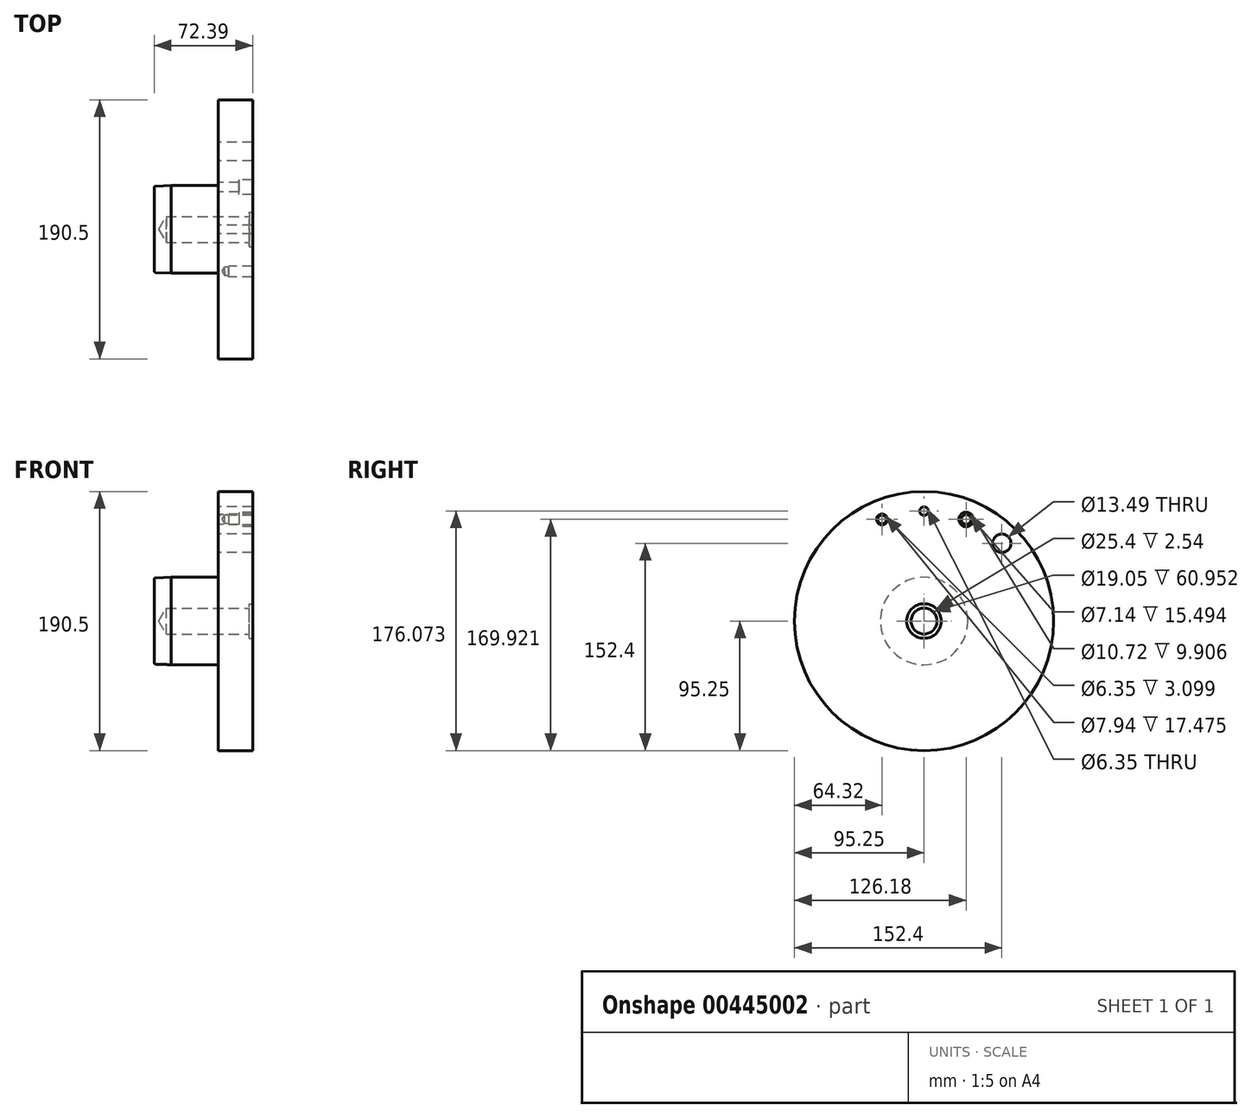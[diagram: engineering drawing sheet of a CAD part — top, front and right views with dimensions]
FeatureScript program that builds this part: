
annotation { "Feature Type Name" : "Feature", "Feature Type Description" : "" }
export const myFeature = defineFeature(function(context is Context, id is Id, definition is map)
    precondition{}
    {
        {
            var Q0;
            Q0=qCreatedBy(makeId("Front.planeOp"),FACE);
            var sketch = newSketch(context, id + "F0", { "sketchPlane" : qUnion([Q0])});
            skLineSegment(sketch, "E0", {"start": v(-46.99, 0) * mm, "end": v(-46.99, 30.46) * mm});
            skArc(sketch, "E1", {"start": v(-47, 30.46) * mm, "mid": v(-46.63, 31.34) * mm, "end": v(-45.76, 31.73) * mm});
            skLineSegment(sketch, "E2", {"start": v(-45.76, 31.73) * mm, "end": v(-34.3, 32.13) * mm});
            skLineSegment(sketch, "E3", {"start": v(-34.29, 32.13) * mm, "end": v(0, 32.13) * mm});
            skLineSegment(sketch, "E4", {"start": v(0, 32.13) * mm, "end": v(0, 95.25) * mm});
            skLineSegment(sketch, "E5", {"start": v(0, 95.25) * mm, "end": v(25.4, 95.25) * mm});
            skLineSegment(sketch, "E6", {"start": v(25.4, 95.25) * mm, "end": v(25.4, 0) * mm});
            skLineSegment(sketch, "E7", {"start": v(25.4, 0) * mm, "end": v(-46.99, 0) * mm});
            skLineSegment(sketch, "E8", {"start": v(0, 0) * mm, "end": v(-66.47, 0) * mm, "construction": true});
            skSolve(sketch);
        }
        {
            var Q0;
            Q0=makeQuery(id+"F0.imprint","IMPRINT",FACE,{"disambiguationData":[TD([[makeQuery(id+"F0.imprint","IMPRINT",EDGE,{"derivedFrom":sQuery(id+"F0.wireOp",EDGE,"E0")}),-1.0]])]});
            var Q1;
            Q1=sQuery(id+"F0.wireOp",EDGE,"E8");
            revolve(context, id + "F1", {"entities" : qUnion([Q0]), "axis" : qUnion([Q1]), "revolveType" : RevolveType.FULL});
        }
        {
            var Q0;
            Q0=qCreatedBy(makeId("Right.planeOp"),FACE);
            var sketch = newSketch(context, id + "F2", { "sketchPlane" : qUnion([Q0])});
            skCircle(sketch, "E9", {"center": v(0, 0) * mm, "radius": 80.82 * mm, "construction": true});
            skCircle(sketch, "E10", {"center": v(57.15, 57.15) * mm, "radius": 6.74 * mm});
            skLineSegment(sketch, "E11", {"start": v(0, 0) * mm, "end": v(57.15, 57.15) * mm, "construction": true});
            skSolve(sketch);
        }
        {
            var Q0;
            Q0=makeQuery(id+"F2.imprint","IMPRINT",FACE,{"disambiguationData":[TD([[makeQuery(id+"F2.imprint","IMPRINT",EDGE,{"derivedFrom":sQuery(id+"F2.wireOp",EDGE,"E10")}),1.0]])]});
            extrude(context, id + "F3", {"entities" : qUnion([Q0]), "operationType" : NewBodyOperationType.REMOVE, "endBound" : BoundingType.UP_TO_NEXT, "depth" : 25.4 * mm});
        }
        {
            var Q0;
            Q0=qCreatedBy(makeId("Front.planeOp"),FACE);
            var sketch = newSketch(context, id + "F4", { "sketchPlane" : qUnion([Q0])});
            skLineSegment(sketch, "E12", {"start": v(0, 0) * mm, "end": v(50.8, 0) * mm, "construction": true});
            skLineSegment(sketch, "E13", {"start": v(-43.81, 0) * mm, "end": v(-38.1, 9.52) * mm});
            skPoint(sketch, "E13.startSnap0", {"position": v(25.4, 0) * mm});
            skLineSegment(sketch, "E14", {"start": v(-38.1, 9.53) * mm, "end": v(22.86, 9.53) * mm});
            skLineSegment(sketch, "E15", {"start": v(25.4, 12.7) * mm, "end": v(25.4, 0) * mm});
            skLineSegment(sketch, "E16", {"start": v(-43.81, 0) * mm, "end": v(25.4, 0) * mm});
            skLineSegment(sketch, "E17", {"start": v(22.86, 9.53) * mm, "end": v(22.86, 12.7) * mm});
            skLineSegment(sketch, "E18", {"start": v(22.86, 12.7) * mm, "end": v(25.4, 12.7) * mm});
            skSolve(sketch);
        }
        {
            var Q0;
            Q0=makeQuery(id+"F4.imprint","IMPRINT",FACE,{"disambiguationData":[TD([[makeQuery(id+"F4.imprint","IMPRINT",EDGE,{"derivedFrom":sQuery(id+"F4.wireOp",EDGE,"E13")}),-1.0]])]});
            var Q1;
            Q1=sQuery(id+"F4.wireOp",EDGE,"E12");
            revolve(context, id + "F5", {"operationType" : NewBodyOperationType.REMOVE, "entities" : qUnion([Q0]), "axis" : qUnion([Q1]), "revolveType" : RevolveType.FULL, "oppositeDirection" : true});
        }
        {
            var Q0;
            Q0=qCreatedBy(makeId("Front.planeOp"),FACE);
            var Q1;
            Q1=sQuery(id+"F0.wireOp",EDGE,"E8");
            cPlane(context, id + "F6", {"entities" : qUnion([Q0, Q1]), "cplaneType" : CPlaneType.LINE_ANGLE, "offset" : 25.4 * mm, "angle" : 22.5 * degree, "width" : 152.4 * mm, "height" : 152.4 * mm});
        }
        {
            var Q0;
            Q0=qCreatedBy(id+"F6.planeOp",FACE);
            var sketch = newSketch(context, id + "F7", { "sketchPlane" : qUnion([Q0])});
            skLineSegment(sketch, "E19", {"start": v(-38.19, 80.82) * mm, "end": v(0, 80.82) * mm, "construction": true});
            skLineSegment(sketch, "E20", {"start": v(0, 80.82) * mm, "end": v(0, 84.4) * mm});
            skLineSegment(sketch, "E21", {"start": v(0, 84.4) * mm, "end": v(-15.5, 84.4) * mm});
            skLineSegment(sketch, "E22", {"start": v(-25.4, 86.18) * mm, "end": v(-25.4, 80.82) * mm});
            skLineSegment(sketch, "E23", {"start": v(-25.4, 80.82) * mm, "end": v(0, 80.82) * mm});
            skLineSegment(sketch, "E24", {"start": v(-15.5, 84.4) * mm, "end": v(-15.5, 86.18) * mm});
            skLineSegment(sketch, "E25", {"start": v(-15.5, 86.18) * mm, "end": v(-25.4, 86.18) * mm});
            skSolve(sketch);
        }
        {
            var Q0;
            Q0=makeQuery(id+"F7.imprint","IMPRINT",FACE,{"disambiguationData":[TD([[makeQuery(id+"F7.imprint","IMPRINT",EDGE,{"derivedFrom":sQuery(id+"F7.wireOp",EDGE,"E20")}),1.0]])]});
            var Q1;
            Q1=sQuery(id+"F7.wireOp",EDGE,"E19");
            revolve(context, id + "F8", {"operationType" : NewBodyOperationType.REMOVE, "entities" : qUnion([Q0]), "axis" : qUnion([Q1]), "revolveType" : RevolveType.FULL, "oppositeDirection" : true});
        }
        {
            var Q0;
            Q0=qCreatedBy(makeId("Front.planeOp"),FACE);
            var Q1;
            Q1=sQuery(id+"F0.wireOp",EDGE,"E8");
            cPlane(context, id + "F9", {"entities" : qUnion([Q0, Q1]), "cplaneType" : CPlaneType.LINE_ANGLE, "offset" : 25.4 * mm, "angle" : 22.5 * degree, "oppositeDirection" : true, "width" : 152.4 * mm, "height" : 152.4 * mm});
        }
        {
            var Q0;
            Q0=qCreatedBy(id+"F9.planeOp",FACE);
            var sketch = newSketch(context, id + "F10", { "sketchPlane" : qUnion([Q0])});
            skLineSegment(sketch, "E26", {"start": v(-40, 80.82) * mm, "end": v(0, 80.82) * mm, "construction": true});
            skLineSegment(sketch, "E27", {"start": v(-25.4, 80.82) * mm, "end": v(-25.4, 84.8) * mm});
            skLineSegment(sketch, "E28", {"start": v(-25.4, 84.8) * mm, "end": v(-7.92, 84.8) * mm});
            skLineSegment(sketch, "E29", {"start": v(-7.92, 84.8) * mm, "end": v(-7.92, 84) * mm});
            skLineSegment(sketch, "E30", {"start": v(-7.92, 84) * mm, "end": v(-4.83, 84) * mm});
            skLineSegment(sketch, "E31", {"start": v(-4.83, 84) * mm, "end": v(-2.92, 80.82) * mm});
            skLineSegment(sketch, "E32", {"start": v(-2.92, 80.82) * mm, "end": v(-25.4, 80.82) * mm});
            skSolve(sketch);
        }
        {
            var Q0;
            Q0=makeQuery(id+"F10.imprint","IMPRINT",FACE,{"disambiguationData":[TD([[makeQuery(id+"F10.imprint","IMPRINT",EDGE,{"derivedFrom":sQuery(id+"F10.wireOp",EDGE,"E27")}),-1.0]])]});
            var Q1;
            Q1=sQuery(id+"F10.wireOp",EDGE,"E26");
            revolve(context, id + "F11", {"operationType" : NewBodyOperationType.REMOVE, "entities" : qUnion([Q0]), "axis" : qUnion([Q1]), "revolveType" : RevolveType.FULL, "oppositeDirection" : true});
        }
        {
            var Q0;
            Q0=qCreatedBy(makeId("Right.planeOp"),FACE);
            var sketch = newSketch(context, id + "F12", { "sketchPlane" : qUnion([Q0])});
            skCircle(sketch, "E33", {"center": v(0, 80.82) * mm, "radius": 3.18 * mm});
            skSolve(sketch);
        }
        {
            var Q0;
            Q0=makeQuery(id+"F12.imprint","IMPRINT",FACE,{"disambiguationData":[TD([[makeQuery(id+"F12.imprint","IMPRINT",EDGE,{"derivedFrom":sQuery(id+"F12.wireOp",EDGE,"E33")}),1.0]])]});
            extrude(context, id + "F13", {"entities" : qUnion([Q0]), "operationType" : NewBodyOperationType.REMOVE, "endBound" : BoundingType.UP_TO_NEXT, "depth" : 25.4 * mm});
        }
    });
